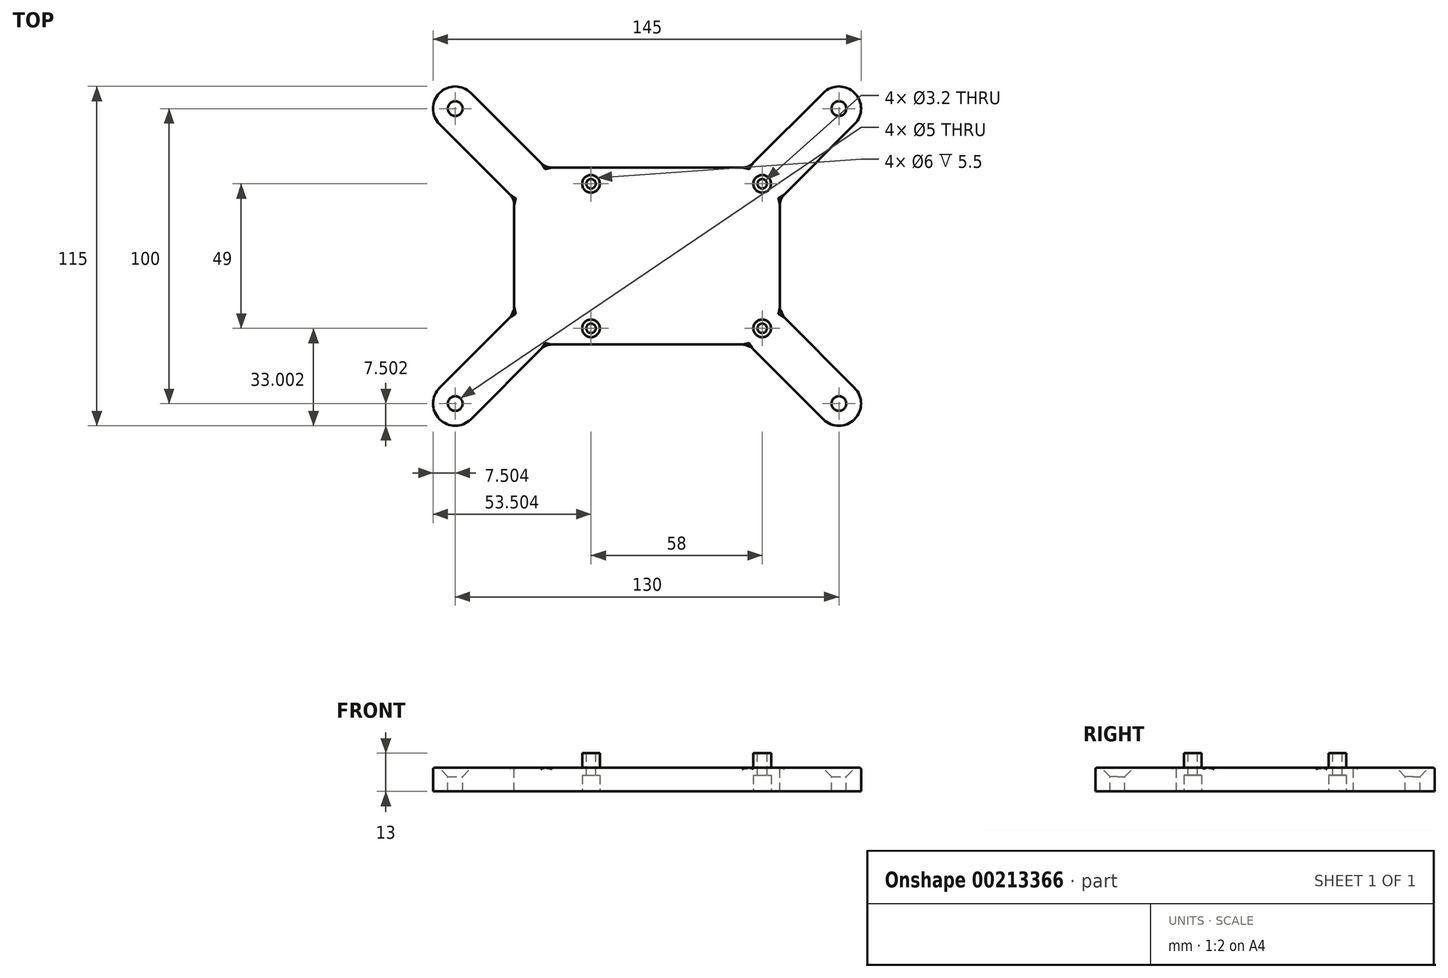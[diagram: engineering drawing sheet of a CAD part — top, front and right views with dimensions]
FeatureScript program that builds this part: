
annotation { "Feature Type Name" : "Feature", "Feature Type Description" : "" }
export const myFeature = defineFeature(function(context is Context, id is Id, definition is map)
    precondition{}
    {
        {
            var Q0;
            Q0=qCreatedBy(makeId("Top.planeOp"),FACE);
            var sketch = newSketch(context, id + "F0", { "sketchPlane" : qUnion([Q0])});
            skLineSegment(sketch, "E0.bottom", {"start": v(-39.06, 40.06) * mm, "end": v(50.94, 40.06) * mm});
            skLineSegment(sketch, "E0.top", {"start": v(-39.06, -19.94) * mm, "end": v(50.94, -19.94) * mm});
            skLineSegment(sketch, "E0.left", {"start": v(-39.06, 40.06) * mm, "end": v(-39.06, -19.94) * mm});
            skLineSegment(sketch, "E0.right", {"start": v(50.94, 40.06) * mm, "end": v(50.94, -19.94) * mm});
            skCircle(sketch, "E1", {"center": v(-33.06, -14.44) * mm, "radius": 1.6 * mm});
            skCircle(sketch, "E2", {"center": v(-33.06, 34.56) * mm, "radius": 1.6 * mm});
            skCircle(sketch, "E3", {"center": v(24.94, -14.44) * mm, "radius": 1.6 * mm});
            skCircle(sketch, "E4", {"center": v(24.94, 34.56) * mm, "radius": 1.6 * mm});
            skArc(sketch, "E5", {"start": v(-64.36, -34.63) * mm, "mid": v(-64.36, -45.24) * mm, "end": v(-53.75, -45.24) * mm});
            skLineSegment(sketch, "E6", {"start": v(-64.36, -34.63) * mm, "end": v(-39.06, -9.33) * mm});
            skLineSegment(sketch, "E7.MirrorCS", {"start": v(-53.75, -45.24) * mm, "end": v(-28.45, -19.94) * mm});
            skCircle(sketch, "E8", {"center": v(-59.06, -39.94) * mm, "radius": 2.5 * mm});
            skArc(sketch, "E9", {"start": v(65.64, -45.24) * mm, "mid": v(76.25, -45.24) * mm, "end": v(76.25, -34.63) * mm});
            skLineSegment(sketch, "E10", {"start": v(65.64, -45.24) * mm, "end": v(65.64, -45.24) * mm});
            skLineSegment(sketch, "E11", {"start": v(40.34, -19.94) * mm, "end": v(65.64, -45.24) * mm});
            skLineSegment(sketch, "E12.MirrorCS", {"start": v(50.94, -9.33) * mm, "end": v(76.25, -34.63) * mm});
            skLineSegment(sketch, "E13", {"start": v(-39.06, 10.06) * mm, "end": v(50.94, 10.06) * mm});
            skCircle(sketch, "E14", {"center": v(70.94, -39.94) * mm, "radius": 2.5 * mm});
            skLineSegment(sketch, "E15.MirrorCS", {"start": v(50.94, 29.46) * mm, "end": v(76.25, 54.76) * mm});
            skLineSegment(sketch, "E16.MirrorCS", {"start": v(40.34, 40.06) * mm, "end": v(65.64, 65.37) * mm});
            skArc(sketch, "E17.MirrorCS", {"start": v(65.64, 65.37) * mm, "mid": v(76.25, 65.37) * mm, "end": v(76.25, 54.76) * mm});
            skCircle(sketch, "E18.MirrorC", {"center": v(70.94, 60.06) * mm, "radius": 2.5 * mm});
            skLineSegment(sketch, "E19.MirrorCS", {"start": v(-53.75, 65.37) * mm, "end": v(-28.45, 40.06) * mm});
            skLineSegment(sketch, "E20.MirrorCS", {"start": v(-64.36, 54.76) * mm, "end": v(-39.06, 29.46) * mm});
            skArc(sketch, "E21.MirrorCS", {"start": v(-64.36, 54.76) * mm, "mid": v(-64.36, 65.37) * mm, "end": v(-53.75, 65.37) * mm});
            skCircle(sketch, "E22.MirrorC", {"center": v(-59.06, 60.06) * mm, "radius": 2.5 * mm});
            skSolve(sketch);
        }
        {
            var Q0;
            Q0=makeQuery(id+"F0.imprint","IMPRINT",FACE,{"disambiguationData":[TD([[makeQuery(id+"F0.imprint","IMPRINT",EDGE,{"derivedFrom":sQuery(id+"F0.wireOp",EDGE,"E2")}),-1.0]])]});
            var Q1;
            Q1=makeQuery(id+"F0.imprint","IMPRINT",FACE,{"disambiguationData":[TD([[makeQuery(id+"F0.imprint","IMPRINT",EDGE,{"derivedFrom":sQuery(id+"F0.wireOp",EDGE,"E1")}),-1.0]])]});
            var Q2;
            Q2=makeQuery(id+"F0.imprint","IMPRINT",FACE,{"disambiguationData":[TD([[makeQuery(id+"F0.imprint","IMPRINT",EDGE,{"derivedFrom":sQuery(id+"F0.wireOp",EDGE,"E9")}),1.0]])]});
            var Q3;
            {var subQ1=sQuery(id+"F0.wireOp",EDGE,"E15.MirrorCS");Q3=makeQuery(id+"F0.imprint","IMPRINT",FACE,{"disambiguationData":[TD([[makeQuery(id+"F0.imprint","IMPRINT",EDGE,{"derivedFrom":subQ1}),1.0]])]});}
            var Q4;
            {var subQ0=sQuery(id+"F0.wireOp",EDGE,"E19.MirrorCS");Q4=makeQuery(id+"F0.imprint","IMPRINT",FACE,{"disambiguationData":[TD([[makeQuery(id+"F0.imprint","IMPRINT",EDGE,{"derivedFrom":subQ0}),-1.0]])]});}
            var Q5;
            Q5=makeQuery(id+"F0.imprint","IMPRINT",FACE,{"disambiguationData":[TD([[makeQuery(id+"F0.imprint","IMPRINT",EDGE,{"derivedFrom":sQuery(id+"F0.wireOp",EDGE,"E5")}),1.0]])]});
            extrude(context, id + "F1", {"entities" : qUnion([Q0, Q1, Q2, Q3, Q4, Q5]), "depth" : 8 * mm});
        }
        {
            var Q0;
            Q0=makeQuery(id+"F1.opExtrude","CAP_EDGE",EDGE,{"disambiguationData":[OSD([sQuery(id+"F0.wireOp",EDGE,"E14")])],"isStart":true});
            var Q1;
            Q1=makeQuery(id+"F1.opExtrude","CAP_EDGE",EDGE,{"disambiguationData":[OSD([sQuery(id+"F0.wireOp",EDGE,"E8")])],"isStart":true});
            var Q2;
            Q2=makeQuery(id+"F1.opExtrude","CAP_EDGE",EDGE,{"disambiguationData":[OSD([sQuery(id+"F0.wireOp",EDGE,"E22.MirrorC")])],"isStart":true});
            var Q3;
            Q3=makeQuery(id+"F1.opExtrude","CAP_EDGE",EDGE,{"disambiguationData":[OSD([sQuery(id+"F0.wireOp",EDGE,"E18.MirrorC")])],"isStart":true});
            chamfer(context, id + "F8", {"entities" : qUnion([Q0, Q1, Q2, Q3]), "width" : 3 * mm, "tangentPropagation" : true});
        }
        {
            var Q0;
            Q0=makeQuery(id+"F1.opExtrude","CAP_FACE",FACE,{"disambiguationData":[OSD([sQuery(id+"F0.wireOp",EDGE,"E0.bottom"),sQuery(id+"F0.wireOp",EDGE,"E0.top"),sQuery(id+"F0.wireOp",EDGE,"E0.left"),sQuery(id+"F0.wireOp",EDGE,"E0.right"),sQuery(id+"F0.wireOp",EDGE,"E1"),sQuery(id+"F0.wireOp",EDGE,"E2"),sQuery(id+"F0.wireOp",EDGE,"E3"),sQuery(id+"F0.wireOp",EDGE,"E4"),sQuery(id+"F0.wireOp",EDGE,"E5"),sQuery(id+"F0.wireOp",EDGE,"E6"),sQuery(id+"F0.wireOp",EDGE,"E7.MirrorCS"),sQuery(id+"F0.wireOp",EDGE,"E8"),sQuery(id+"F0.wireOp",EDGE,"E9"),sQuery(id+"F0.wireOp",EDGE,"E11"),sQuery(id+"F0.wireOp",EDGE,"E12.MirrorCS"),sQuery(id+"F0.wireOp",EDGE,"E14"),sQuery(id+"F0.wireOp",EDGE,"E15.MirrorCS"),sQuery(id+"F0.wireOp",EDGE,"E16.MirrorCS"),sQuery(id+"F0.wireOp",EDGE,"E17.MirrorCS"),sQuery(id+"F0.wireOp",EDGE,"E18.MirrorC"),sQuery(id+"F0.wireOp",EDGE,"E19.MirrorCS"),sQuery(id+"F0.wireOp",EDGE,"E20.MirrorCS"),sQuery(id+"F0.wireOp",EDGE,"E21.MirrorCS"),sQuery(id+"F0.wireOp",EDGE,"E22.MirrorC")])],"isStart":true});
            var sketch = newSketch(context, id + "F2", { "sketchPlane" : qUnion([Q0])});
            skCircle(sketch, "E23", {"center": v(-33.06, 14.44) * mm, "radius": 3 * mm});
            skCircle(sketch, "E24", {"center": v(-33.06, -34.56) * mm, "radius": 3 * mm});
            skCircle(sketch, "E25", {"center": v(24.94, -34.56) * mm, "radius": 3 * mm});
            skCircle(sketch, "E26", {"center": v(24.94, 14.44) * mm, "radius": 3 * mm});
            skSolve(sketch);
        }
        {
            var Q0;
            Q0=makeQuery(id+"F2.imprint","IMPRINT",FACE,{"disambiguationData":[TD([[makeQuery(id+"F2.imprint","IMPRINT",EDGE,{"derivedFrom":sQuery(id+"F2.wireOp",EDGE,"E24")}),1.0]])]});
            var Q1;
            Q1=makeQuery(id+"F2.imprint","IMPRINT",FACE,{"disambiguationData":[TD([[makeQuery(id+"F2.imprint","IMPRINT",EDGE,{"derivedFrom":sQuery(id+"F2.wireOp",EDGE,"E25")}),1.0]])]});
            var Q2;
            Q2=makeQuery(id+"F2.imprint","IMPRINT",FACE,{"disambiguationData":[TD([[makeQuery(id+"F2.imprint","IMPRINT",EDGE,{"derivedFrom":sQuery(id+"F2.wireOp",EDGE,"E26")}),1.0]])]});
            var Q3;
            Q3=makeQuery(id+"F2.imprint","IMPRINT",FACE,{"disambiguationData":[TD([[makeQuery(id+"F2.imprint","IMPRINT",EDGE,{"derivedFrom":sQuery(id+"F2.wireOp",EDGE,"E23")}),1.0]])]});
            extrude(context, id + "F3", {"entities" : qUnion([Q0, Q1, Q2, Q3]), "operationType" : NewBodyOperationType.ADD, "depth" : 5 * mm});
        }
        {
            var Q0;
            Q0=makeQuery(id+"F1.opExtrude","CAP_FACE",FACE,{"disambiguationData":[OSD([sQuery(id+"F0.wireOp",EDGE,"E0.bottom"),sQuery(id+"F0.wireOp",EDGE,"E0.top"),sQuery(id+"F0.wireOp",EDGE,"E0.left"),sQuery(id+"F0.wireOp",EDGE,"E0.right"),sQuery(id+"F0.wireOp",EDGE,"E1"),sQuery(id+"F0.wireOp",EDGE,"E2"),sQuery(id+"F0.wireOp",EDGE,"E3"),sQuery(id+"F0.wireOp",EDGE,"E4"),sQuery(id+"F0.wireOp",EDGE,"E5"),sQuery(id+"F0.wireOp",EDGE,"E6"),sQuery(id+"F0.wireOp",EDGE,"E7.MirrorCS"),sQuery(id+"F0.wireOp",EDGE,"E8"),sQuery(id+"F0.wireOp",EDGE,"E9"),sQuery(id+"F0.wireOp",EDGE,"E11"),sQuery(id+"F0.wireOp",EDGE,"E12.MirrorCS"),sQuery(id+"F0.wireOp",EDGE,"E14"),sQuery(id+"F0.wireOp",EDGE,"E15.MirrorCS"),sQuery(id+"F0.wireOp",EDGE,"E16.MirrorCS"),sQuery(id+"F0.wireOp",EDGE,"E17.MirrorCS"),sQuery(id+"F0.wireOp",EDGE,"E18.MirrorC"),sQuery(id+"F0.wireOp",EDGE,"E19.MirrorCS"),sQuery(id+"F0.wireOp",EDGE,"E20.MirrorCS"),sQuery(id+"F0.wireOp",EDGE,"E21.MirrorCS"),sQuery(id+"F0.wireOp",EDGE,"E22.MirrorC")])],"isStart":true});
            fillet(context, id + "F4", {"entities" : qUnion([Q0]), "radius" : .5 * mm, "tangentPropagation" : true, "allowEdgeOverflow" : false});
        }
        {
            var Q0;
            Q0=makeQuery(id+"F1.opExtrude","SWEPT_EDGE",EDGE,{"disambiguationData":[OSD([sQuery(id+"F0.wireOp",EDGE,"E0.top"),sQuery(id+"F0.wireOp",EDGE,"E11")])]});
            var Q1;
            Q1=makeQuery(id+"F1.opExtrude","SWEPT_EDGE",EDGE,{"disambiguationData":[OSD([sQuery(id+"F0.wireOp",EDGE,"E0.top"),sQuery(id+"F0.wireOp",EDGE,"E7.MirrorCS")])]});
            var Q2;
            Q2=makeQuery(id+"F1.opExtrude","SWEPT_EDGE",EDGE,{"disambiguationData":[OSD([sQuery(id+"F0.wireOp",EDGE,"E0.left"),sQuery(id+"F0.wireOp",EDGE,"E6")])]});
            var Q3;
            Q3=makeQuery(id+"F1.opExtrude","SWEPT_EDGE",EDGE,{"disambiguationData":[OSD([sQuery(id+"F0.wireOp",EDGE,"E0.left"),sQuery(id+"F0.wireOp",EDGE,"E20.MirrorCS")])]});
            var Q4;
            Q4=makeQuery(id+"F1.opExtrude","SWEPT_EDGE",EDGE,{"disambiguationData":[OSD([sQuery(id+"F0.wireOp",EDGE,"E0.bottom"),sQuery(id+"F0.wireOp",EDGE,"E19.MirrorCS")])]});
            var Q5;
            Q5=makeQuery(id+"F1.opExtrude","SWEPT_EDGE",EDGE,{"disambiguationData":[OSD([sQuery(id+"F0.wireOp",EDGE,"E0.bottom"),sQuery(id+"F0.wireOp",EDGE,"E16.MirrorCS")])]});
            var Q6;
            Q6=makeQuery(id+"F1.opExtrude","SWEPT_EDGE",EDGE,{"disambiguationData":[OSD([sQuery(id+"F0.wireOp",EDGE,"E0.right"),sQuery(id+"F0.wireOp",EDGE,"E12.MirrorCS")])]});
            var Q7;
            Q7=makeQuery(id+"F1.opExtrude","SWEPT_EDGE",EDGE,{"disambiguationData":[OSD([sQuery(id+"F0.wireOp",EDGE,"E0.right"),sQuery(id+"F0.wireOp",EDGE,"E15.MirrorCS")])]});
            fillet(context, id + "F9", {"entities" : qUnion([Q0, Q1, Q2, Q3, Q4, Q5, Q6, Q7]), "radius" : 5 * mm, "tangentPropagation" : true, "allowEdgeOverflow" : false});
        }
        {
            var Q0;
            Q0=makeQuery(id+"F1.opExtrude","SWEPT_BODY",BODY,{"disambiguationData":[OSD([sQuery(id+"F0.wireOp",EDGE,"E0.bottom"),sQuery(id+"F0.wireOp",EDGE,"E0.top"),sQuery(id+"F0.wireOp",EDGE,"E0.left"),sQuery(id+"F0.wireOp",EDGE,"E0.right"),sQuery(id+"F0.wireOp",EDGE,"E1"),sQuery(id+"F0.wireOp",EDGE,"E2"),sQuery(id+"F0.wireOp",EDGE,"E3"),sQuery(id+"F0.wireOp",EDGE,"E4"),sQuery(id+"F0.wireOp",EDGE,"E5"),sQuery(id+"F0.wireOp",EDGE,"E6"),sQuery(id+"F0.wireOp",EDGE,"E7.MirrorCS"),sQuery(id+"F0.wireOp",EDGE,"E8"),sQuery(id+"F0.wireOp",EDGE,"E9"),sQuery(id+"F0.wireOp",EDGE,"E11"),sQuery(id+"F0.wireOp",EDGE,"E12.MirrorCS"),sQuery(id+"F0.wireOp",EDGE,"E14"),sQuery(id+"F0.wireOp",EDGE,"E15.MirrorCS"),sQuery(id+"F0.wireOp",EDGE,"E16.MirrorCS"),sQuery(id+"F0.wireOp",EDGE,"E17.MirrorCS"),sQuery(id+"F0.wireOp",EDGE,"E18.MirrorC"),sQuery(id+"F0.wireOp",EDGE,"E19.MirrorCS"),sQuery(id+"F0.wireOp",EDGE,"E20.MirrorCS"),sQuery(id+"F0.wireOp",EDGE,"E21.MirrorCS"),sQuery(id+"F0.wireOp",EDGE,"E22.MirrorC")])]});
            var Q1;
            Q1=makeQuery(id+"F1.opExtrude","CAP_EDGE",EDGE,{"disambiguationData":[OSD([sQuery(id+"F0.wireOp",EDGE,"E0.top")])],"isStart":false});
            var Q2;
            {var subQ0=sQuery(id+"F0.wireOp",EDGE,"E0.right");Q2=makeQuery(id+"F4.opFillet","BLEND_EDGE",EDGE,{"blendedFrom":[makeQuery(id+"F1.opExtrude","CAP_EDGE",EDGE,{"disambiguationData":[OSD([subQ0])],"isStart":true}),makeQuery(id+"F1.opExtrude","SWEPT_FACE",FACE,{"disambiguationData":[OSD([subQ0])]})],"blendedInto":[makeQuery(id+"F1.opExtrude","SWEPT_FACE",FACE,{"disambiguationData":[OSD([subQ0])]})]});}
            transform(context, id + "F5", {"entities" : qUnion([Q0]), "transformType" : TransformType.ROTATION, "transformAxis" : qUnion([Q2]), "angle" : 180 * degree, "makeCopy" : false});
        }
        {
            var Q0;
            Q0=makeQuery(id+"F1.opExtrude","CAP_FACE",FACE,{"disambiguationData":[OSD([sQuery(id+"F0.wireOp",EDGE,"E0.bottom"),sQuery(id+"F0.wireOp",EDGE,"E0.top"),sQuery(id+"F0.wireOp",EDGE,"E0.left"),sQuery(id+"F0.wireOp",EDGE,"E0.right"),sQuery(id+"F0.wireOp",EDGE,"E1"),sQuery(id+"F0.wireOp",EDGE,"E2"),sQuery(id+"F0.wireOp",EDGE,"E3"),sQuery(id+"F0.wireOp",EDGE,"E4"),sQuery(id+"F0.wireOp",EDGE,"E5"),sQuery(id+"F0.wireOp",EDGE,"E6"),sQuery(id+"F0.wireOp",EDGE,"E7.MirrorCS"),sQuery(id+"F0.wireOp",EDGE,"E8"),sQuery(id+"F0.wireOp",EDGE,"E9"),sQuery(id+"F0.wireOp",EDGE,"E11"),sQuery(id+"F0.wireOp",EDGE,"E12.MirrorCS"),sQuery(id+"F0.wireOp",EDGE,"E14"),sQuery(id+"F0.wireOp",EDGE,"E15.MirrorCS"),sQuery(id+"F0.wireOp",EDGE,"E16.MirrorCS"),sQuery(id+"F0.wireOp",EDGE,"E17.MirrorCS"),sQuery(id+"F0.wireOp",EDGE,"E18.MirrorC"),sQuery(id+"F0.wireOp",EDGE,"E19.MirrorCS"),sQuery(id+"F0.wireOp",EDGE,"E20.MirrorCS"),sQuery(id+"F0.wireOp",EDGE,"E21.MirrorCS"),sQuery(id+"F0.wireOp",EDGE,"E22.MirrorC")])],"isStart":false});
            var sketch = newSketch(context, id + "F6", { "sketchPlane" : qUnion([Q0])});
            skCircle(sketch, "E27", {"center": v(76.94, 14.44) * mm, "radius": 3 * mm});
            skCircle(sketch, "E28", {"center": v(134.94, 14.44) * mm, "radius": 3 * mm});
            skCircle(sketch, "E29", {"center": v(76.94, -34.56) * mm, "radius": 3 * mm});
            skCircle(sketch, "E30", {"center": v(134.94, -34.56) * mm, "radius": 3 * mm});
            skSolve(sketch);
        }
        {
            var Q0;
            Q0=makeQuery(id+"F6.imprint","IMPRINT",FACE,{"disambiguationData":[TD([[makeQuery(id+"F6.imprint","IMPRINT",EDGE,{"derivedFrom":sQuery(id+"F6.wireOp",EDGE,"E27")}),1.0]])]});
            var Q1;
            Q1=makeQuery(id+"F6.imprint","IMPRINT",FACE,{"disambiguationData":[TD([[makeQuery(id+"F6.imprint","IMPRINT",EDGE,{"derivedFrom":sQuery(id+"F6.wireOp",EDGE,"E29")}),1.0]])]});
            var Q2;
            Q2=makeQuery(id+"F6.imprint","IMPRINT",FACE,{"disambiguationData":[TD([[makeQuery(id+"F6.imprint","IMPRINT",EDGE,{"derivedFrom":sQuery(id+"F6.wireOp",EDGE,"E30")}),1.0]])]});
            var Q3;
            Q3=makeQuery(id+"F6.imprint","IMPRINT",FACE,{"disambiguationData":[TD([[makeQuery(id+"F6.imprint","IMPRINT",EDGE,{"derivedFrom":sQuery(id+"F6.wireOp",EDGE,"E28")}),1.0]])]});
            var Q4;
            {var subQ0=sQuery(id+"F6.wireOp",EDGE,"bde0d42f-f172-4950-98d7-3b07549329f4");Q4=makeQuery(id+"F6.imprint","IMPRINT",FACE,{"disambiguationData":[TD([[makeQuery(id+"F6.imprint","IMPRINT",EDGE,{"derivedFrom":subQ0}),-1.0]])]});}
            var Q5;
            {var subQ0=sQuery(id+"F6.wireOp",EDGE,"32870eeb-38ea-47ec-94e7-3c3fa31d8c02");Q5=makeQuery(id+"F6.imprint","IMPRINT",FACE,{"disambiguationData":[TD([[makeQuery(id+"F6.imprint","IMPRINT",EDGE,{"derivedFrom":subQ0}),-1.0]])]});}
            var Q6;
            {var subQ0=sQuery(id+"F6.wireOp",EDGE,"0632fe3a-0250-48bc-8a81-9cea044da1e7");Q6=makeQuery(id+"F6.imprint","IMPRINT",FACE,{"disambiguationData":[TD([[makeQuery(id+"F6.imprint","IMPRINT",EDGE,{"derivedFrom":subQ0}),1.0]])]});}
            var Q7;
            {var subQ0=sQuery(id+"F6.wireOp",EDGE,"47f4bdf8-6caa-4d5e-8825-ec971f9a2b86");Q7=makeQuery(id+"F6.imprint","IMPRINT",FACE,{"disambiguationData":[TD([[makeQuery(id+"F6.imprint","IMPRINT",EDGE,{"derivedFrom":subQ0}),-1.0]])]});}
            extrude(context, id + "F7", {"entities" : qUnion([Q0, Q1, Q2, Q3, Q4, Q5, Q6, Q7]), "operationType" : NewBodyOperationType.REMOVE, "oppositeDirection" : true, "depth" : 5.5 * mm});
        }
    });
